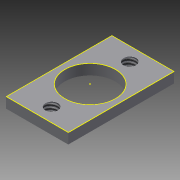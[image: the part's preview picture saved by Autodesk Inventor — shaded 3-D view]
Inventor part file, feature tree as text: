
AUTODESK INVENTOR PART (.ipt)
format: ipt  version: 2013 (Build 170138000, 138)  size: 93,696 bytes
history: native  units: in
note: dims shown in document units (in); Inventor stores cm internally (conversion verified against a paired STEP export)
features: sketch x3, extrude x2, hole x2
ambient origin geometry x8: Origin, YZ Plane, XZ Plane, XY Plane, X Axis, Y Axis, Z Axis, Center Point
feature tree (7):
  extrude  "Extrusion2"  Depth=0.3937in
  extrude  "Extrusion3"  Depth=0.189in
  sketch  "Sketch4"  dims[d7=0.0394in d8=0.0in d9=0.0512in d10=0.1181in d11=0.0465in d12=0.0394in d13=0.1575in d14=0.0787in d15=90.0deg d16=0.315in d17=0.8108in d18=0.1181in d19=0.0512in d20=0.0465in d21=0.0394in d22=0.1575in d23=0.0787in d24=90.0deg d25=0.315in d26=0.8108in]
  hole  "Hole1"  [1 undecoded]
  hole  "Hole2"  [1 undecoded]
  sketch  "Sketch2"  dims[d2=0.2315in d3=0.3937in]
  sketch  "Sketch3"  dims[d4=0.0394in d5=0.0in d6=0.189in]
note: 2 required parameter values undecoded (feature->parameter linkage not recoverable at this tier; creation-order binding heuristic only, values carry confidence <= 0.55)
